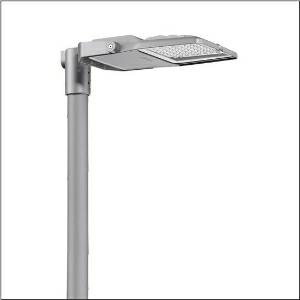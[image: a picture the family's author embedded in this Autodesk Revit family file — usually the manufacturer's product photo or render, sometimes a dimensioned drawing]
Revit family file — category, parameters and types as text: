
# Revit family: floodlight_fl_21_mini___pl64_5xa7771d4e3a_b8d3
name_source: partatom
category: Lighting Fixtures
units: mm (PartAtom-declared; Revit-internal decimal feet)

## family parameters
Cut with Voids When Loaded = No
Host = Face
Light Source = No
Part Type = Normal
Room Calculation Point = No
Round Connector Dimension = Use Diameter
Shared = No

## types (1)
- --- (1 x LED, 17970 lm, 143 W, 4000K)
    Apparent Load = 143 VA
    CIE Flux Codes = 28 80 98 100 100
    Color Rendering = 70
    Color Temperature = 4000K
    Default Elevation = 1800 mm
    Description = Floodlight FL 21 mini, floodlight, primary light control with lens, of PMMA, primary optical cover: protective disc, of toughened safety glass, transparent, light distribution: PL64, light emission: direct distribution, installation type: surface-mounted, LED, High Power LED, rated luminous flux: 17.970lm, luminous efficacy: 126lm/W, light colour: 740, colour temperature: 4000K, control gear: ECG iQ, control: Auto-Match, Temp-Guard, Lumen-Switch, Night-Set, Smart-Wire, Light-Fading, Desk-Remote (wireless, voltage-free reading and setting of iQ features in the workshop via application-optimized NFC function/RFID function), optimised constant luminous flux control (CLO 2.0), with terminal, 6-pole, mains connection: 220..240V, AC, 50/60Hz, start of lifetime: 143W, end of lifetime: 152W, reduction: 61W, luminaire housing, of diecast aluminium, powder-coated, Siteco® metallic grey (DB 702S), corrosivity category C5 according to DIN EN ISO 12944, mast bracket, of steel, galvanised, powder-coated, Siteco® metallic grey (DB 702S), protection rating (complete): IP66, insulation class (complete): insulation class II (safety insulation), certification: CE, ENEC, VDE, protection symbol: D, impact resistance: IK08, permissible operating ambient temperature: -40..+40°C, permissible operating ambient temperature for outdoor applications: -40..+50°C, standard: DIN EN 12944, packaging unit: 1 piece

Light Distribution: PL64
    Height = 70 mm
    Lamp = 1 x LED
    Lamp Light Flux = 17970 lm
    Lamp Power = 143 W
    Lamp count = 1
    Length = 485 mm
    Luminous efficacy = 126 lm/W
    Manufacturer = Siteco
    ModVariant = No
    Model = 5XA7771D4E3A
    Number of Poles = 1
    OnlyDefault = Yes
    Power Factor = 1
    Product Name = Floodlight FL 21 mini | PL64
    Product group = floodlight | pylon top
    ProductGroupID = 6101
    Protection Class = Protection class II
    Protection Degree = IP 66
    RLX_Detail_Level = 1
    RlxData = <blob elided: 101333 chars, md5=bf06d2d9>
    Socket = socket
    Standby Power = 0 W
    System Light Flux = 17970 lm
    System Power = 143 W
    Type Comments = factory setting: luminous flux: 100 % | dim-lin: 254 | 730 mA
    Type Image = l_1007125.jpg
    URL = http://relux.com
    VarID = @adj_077005
    Voltage = 0 V
    Weight = 0.00 kg
    Width = 337 mm

## geometry (parser evidence)
native form markers: Blend x4, Sweep x13
no freeform markers — native parametric forms only
